# Revit family: 2019_ES_Ventana_QSystems_Q67+_1-Hoja
name_source: partatom
category: Windows
units: mm (PartAtom-declared; Revit-internal decimal feet)

## family parameters
Always vertical = Yes
Cut with Voids When Loaded = No
Host = Wall
OmniClass Number = 23.30.20.00
OmniClass Title = Windows
Room Calculation Point = No
Shared = No

## types (4) — shared parameters
Abatible = No
Acabado = Anodizado, lacado y acabados
Acristalamiento = Cristal - Vidrio claro templado
Altura Real = 1480.000 mm
Altura de antepecho por defecto = 700.000 mm
Altura maxima = 2500.000 mm
Altura minima = 600.000 mm
AnchoMarcoPerimetral = 89.100 mm
AnchoPoliamidaHoja = 30.000 mm
AnchoPoliamidaMarco = 30.000 mm
Anchura Maxima = 1700.000 mm
Anchura Minima = 100.000 mm
Anchura Real = 1230.000 mm
Area = 1.820 m²
Autor = Bimetica Parametric Design Services, S.L.
BIMsupport = https://bimsupport.info
COBieCategoria = IfcWindow
Catálogo (URL) = https://qsystemsaluminio.com
CerramientoExterior = Yes
Clasificacion acustica = 38 (-1,-4) dB
ConfiguracionPoliamidas = 273800 - 493800 - 493700
ControlHumos = No
CosteEnergeticoMj = 0 J
Description = Ventana Practicable/ Oscilo-Batiente de una hoja de Aluminio con RPT, modelo Q67 de QSystems
EspesorPerfilesAluminio = 1.500 mm
EstanqueidadAgua = E1200
FechaEmisionElementoBIM = 03/12/2021
FechaVencimientoElementoBIM = 03/12/2022
Fraccion de area de acristalamiento = 0.829268
GrosorAcristalamiento = 24.000 mm
GrosorAcristalamiento Real = 24.000 mm
GrosorHoja = 67.000 mm
GrosorMarco = 60.000 mm
GrosorMaximoAcristalamiento = 46.000 mm
GrosorMinimoAcristalamiento = 12.000 mm
Gubimclass Codigo = 30.10.20.10
Gubimclass Titulo = Ventanas de fachadas
Height = 1480.000 mm
Historial = (RVT2019) Actualziación a estándar GDO-BIM y datos. (RVT2015) Creación del Elemento.
IfcExportAs = IfcWindow
InformacionTecnica = https://qsystemsaluminio.com
Intercalario = Technoform Warm Edge
Manija = Yes
Manufacturer = QSystems
Marcado CE = No
Marco = Aluminio
MasterformatCodigo = 08 50 00
MasterformatTitulo = Windows
Motorizada = No
Numero de Licencia = XXX-XXXX9536
OmniclassCodigo = 23-17 13 00
OmniclassTitulo = Window
Perimetro = 5420
PermeabilidadAlAire = Clase 4
Peso = 0.00 kg
PesoMáximoDeLaHoja = 0.00 kg
Plataforma descaga contenido BIM = www.bimetica.com
Poliamida = Technoform polyamide
Porcentaje materiales reciclados = 0.00%
Profundidad = 0.000 mm
PuntoDeContacto = QSystems
Referencia = Q67+
ReferenciaContacto = QSystems
RepisaExterior = Yes
RepisaInterior = Yes
ResistenciaAlViento = Clase C5
SalidaEmergencia = No
Serie = Q67+
TelefonoContacto = +34 91 895 58 00
Titular = Alueuropa S.A.
UNSPSCCodigo = 30171612
UNSPSCTitulo = Projected windows
URL = http://qsystemsaluminio.com
URL Perfil BIM = https://bimetica.com
URL Poliamida = http://www.technoform.es
URL Poliamida - Catálogo = http://www.technoform.com
URLProducto = https://qsystemsaluminio.com
Uniclass2.0Codigo = Ss_15_50_25
Uniclass2.0Titulo = Doors, Windows And Glazing Survey Systems
Version = RVT2019
Version Estandar GDO-BIM = GDO-BIM V02
Wall Closure = By host
Width = 1230.000 mm
Y𝑔 = 0.11
𝐴𝑓 = 0.451 m²
𝐴𝑔 = 1.369 m²
𝑈𝑔 = 1.5
𝑙𝑔 = 4707.200 mm
zero-valued in all types: AcidificacionAtmosferica, AcidificacionAtmosfericaPorUnidad, AguaConsumida, AguaConsumidaPorUnidad, CambioClimatico, CambioClimaticoPorUnidad, CosteEnergeticoKwh, CosteMantenimiento, DestruccionCapaOzonoEstratosferica, DestruccionCapaOzonoEstratosfericaPorUnidad, EmisionCO2, Energia consumida, EnergiaNoRenovableConsumida, EnergiaNoRenovableConsumidaPorUnidad, EnergiaPrimariaTotalConsumida, EnergiaPrimariaTotalConsumidaPorUnidad, EnergiaRenovableConsumida, EnergiaRenovableConsumidaPorUnidad, Eutrofizacion, EutrofizacionPorUnidad, FactorSolarModificado, FactorSombra, FaltaDeRecursos, FaltaDeRecursosPorUnidad, FormacionFotoquimicaOzono, FormacionFotoquimicaOzonoPorUnidad, Infiltracion, ResiduoInerte, ResiduoInertePorUnidad, ResiduoRadioactivo, ResiduoRadioactivoPorUnidad, ResiduosNoPeligrosos, ResiduosNoPeligrososPorUnidad, ResiduosPeligrosos, ResiduosPeligrososPorUnidad

## per-type parameters (varying)
| type | Analytic Construction | Espuma | Heat Transfer Coefficient (U) | IfcExportType | Model | Operation | OsciloBatiente | Practicable | Solar Heat Gain Coefficient | Thermal Resistance (R) | Transmitancia termica | Visual Light Transmittance | 𝑈𝑓 | 𝑈𝑤 |
| 1230x1480 - Practicable | 1/2 in Pilkington single glazing |  | 6.2426 W/(m²·K) | Practicble | Ventana Q67+ - 1 Hoja Practicble | Practicable. Ventana Practicable de una hoja con apertura Interior | No | Yes | 0.81 | 0.1602 (m²·K)/W | 2.0075 W/(m²·K) | 0.88 | 2.4 | 2.007494 |
| 1230x1480 - Oscilobatiente | 1/4 in Pilkington single glazing |  | 6.7018 W/(m²·K) | Oscilobatiente | Ventana Q67+ - 1 Hoja Oscilobatiente | Oscilobatiente. Ventana oscilobatiente de una hoja con apertura Interior | Yes | No | 0.86 | 0.1492 (m²·K)/W | 2.0075 W/(m²·K) | 0.9 | 2.4 | 2.007494 |
| 1230x1480 - Practicable con Espuma | 1/2 in Pilkington single glazing | Espuma de conductividad 0.021W/mK entre varillas.
Espuma de conductividad 0.034W/mK en el galce del vidrio y en el marco. | 6.2426 W/(m²·K) | Practicable | Ventana Q67+ - 1 Hoja Practicable | Practicable. Ventana Practicable de una hoja con apertura Interior | No | Yes | 0.81 | 0.1602 (m²·K)/W | 1.9331 W/(m²·K) | 0.88 | 2.1 | 1.933142 |
| 1230x1480 - Oscilobatiente con Espuma | 1/4 in Pilkington single glazing | Espuma de conductividad 0.021W/mK entre varillas.
Espuma de conductividad 0.034W/mK en el galce del vidrio y en el marco. | 6.7018 W/(m²·K) | Oscilobatiente | Ventana Q67+ - 1 Hoja Oscilobatiente | Oscilobatiente. Ventana oscilobatiente de una hoja con apertura Interior | Yes | No | 0.86 | 0.1492 (m²·K)/W | 1.9331 W/(m²·K) | 0.9 | 2.1 | 1.933142 |

## geometry (parser evidence)
native form markers: Blend x2
no freeform markers — native parametric forms only
